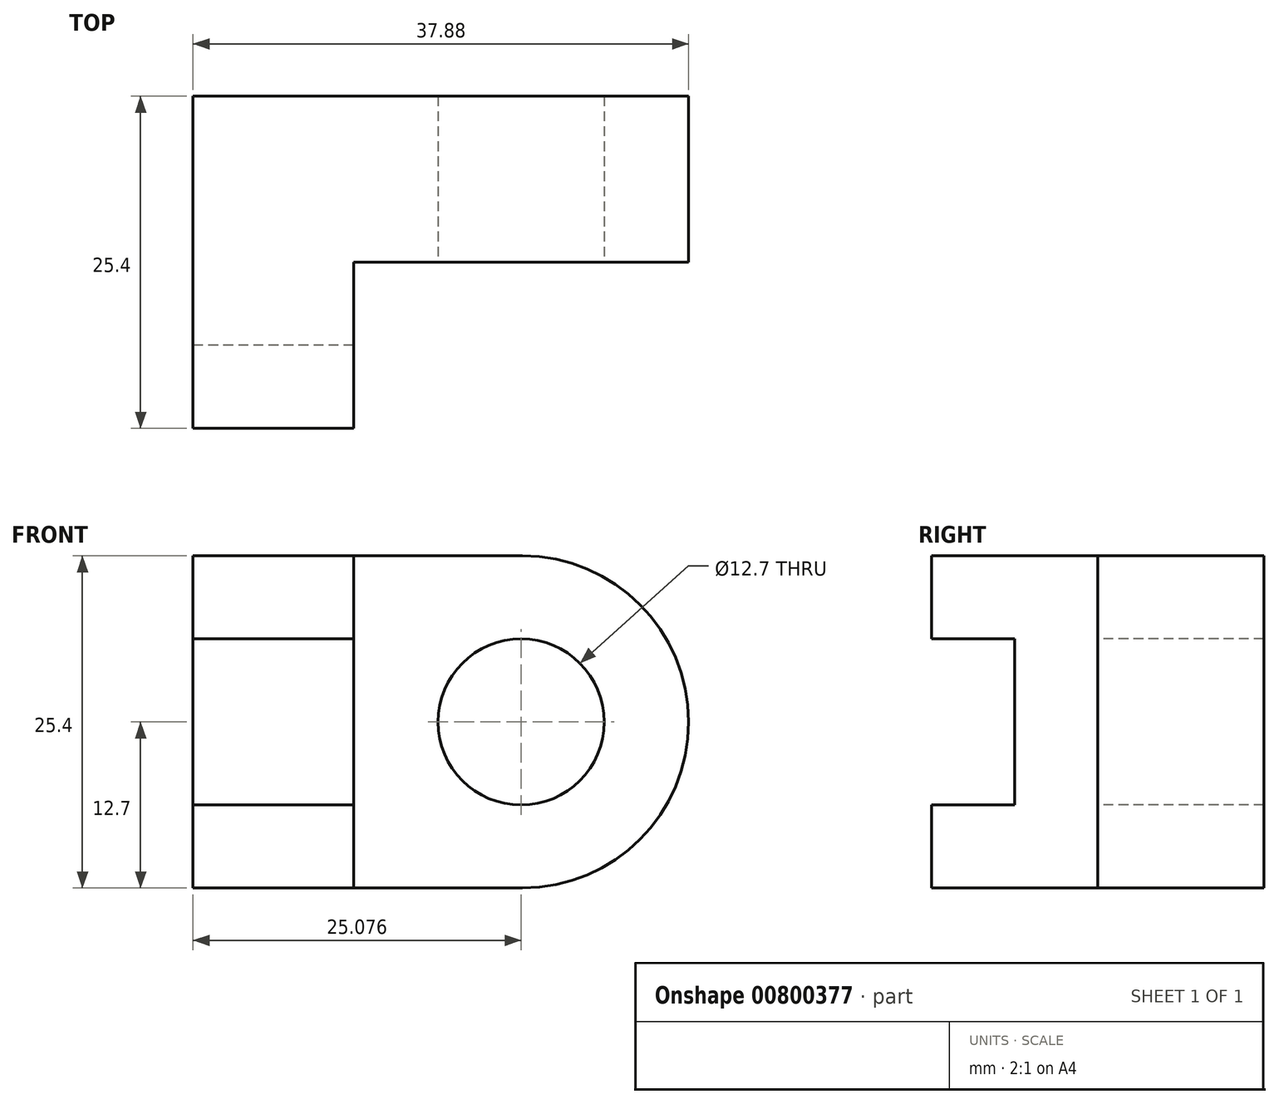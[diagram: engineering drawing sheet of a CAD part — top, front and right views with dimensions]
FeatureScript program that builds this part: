
annotation { "Feature Type Name" : "Feature", "Feature Type Description" : "" }
export const myFeature = defineFeature(function(context is Context, id is Id, definition is map)
    precondition{}
    {
        {
            var Q0;
            Q0=qCreatedBy(makeId("Front.planeOp"),FACE);
            var sketch = newSketch(context, id + "F0", { "sketchPlane" : qUnion([Q0])});
            skLineSegment(sketch, "E0", {"start": v(0, 0) * mm, "end": v(0, 25.4) * mm});
            skLineSegment(sketch, "E1", {"start": v(0, 0) * mm, "end": v(38.1, 0) * mm});
            skLineSegment(sketch, "E2", {"start": v(38.1, 0) * mm, "end": v(38.1, 25.4) * mm});
            skLineSegment(sketch, "E3", {"start": v(0, 25.4) * mm, "end": v(38.1, 25.4) * mm});
            skLineSegment(sketch, "E4", {"start": v(0, 25.4) * mm, "end": v(12.7, 25.4) * mm});
            skSolve(sketch);
        }
        {
            var Q0;
            Q0=makeQuery(id+"F0.imprint","IMPRINT",FACE,{"disambiguationData":[TD([[makeQuery(id+"F0.imprint","IMPRINT",EDGE,{"derivedFrom":sQuery(id+"F0.wireOp",EDGE,"E0")}),-1.0]])]});
            extrude(context, id + "F1", {"entities" : qUnion([Q0]), "depth" : 25.4 * mm, "offsetDistance" : 25.4 * mm});
        }
        {
            var Q0;
            Q0=makeQuery(id+"F1.opExtrude","SWEPT_FACE",FACE,{"disambiguationData":[OSD([sQuery(id+"F0.wireOp",EDGE,"E3"),sQuery(id+"F0.wireOp",EDGE,"E4")])]});
            var sketch = newSketch(context, id + "F2", { "sketchPlane" : qUnion([Q0])});
            skLineSegment(sketch, "E5", {"start": v(12.27, -25.4) * mm, "end": v(12.27, -12.7) * mm});
            skLineSegment(sketch, "E6", {"start": v(12.27, -12.7) * mm, "end": v(38.1, -12.7) * mm});
            skSolve(sketch);
        }
        {
            var Q0;
            {var subQ0=sQuery(id+"F2.wireOp",EDGE,"E5");Q0=makeQuery(id+"F2.imprint","IMPRINT",FACE,{"disambiguationData":[TD([[makeQuery(id+"F2.imprint","IMPRINT",EDGE,{"derivedFrom":subQ0}),-1.0]])]});}
            extrude(context, id + "F3", {"entities" : qUnion([Q0]), "operationType" : NewBodyOperationType.REMOVE, "oppositeDirection" : true, "depth" : 25.4 * mm, "offsetDistance" : 25.4 * mm});
        }
        {
            var Q0;
            Q0=makeQuery(id+"F3.boolean.opBoolean","COPY",FACE,{"derivedFrom":makeQuery(id+"F3.opExtrude","SWEPT_FACE",FACE,{"disambiguationData":[OSD([sQuery(id+"F2.wireOp",EDGE,"E6")])]})});
            var sketch = newSketch(context, id + "F4", { "sketchPlane" : qUnion([Q0])});
            skLineSegment(sketch, "E7", {"start": v(12.27, 25.4) * mm, "end": v(25.18, 25.4) * mm});
            skLineSegment(sketch, "E8", {"start": v(25.18, 25.4) * mm, "end": v(25.18, 0) * mm});
            skArc(sketch, "E9", {"start": v(25.18, 0) * mm, "mid": v(37.88, 12.7) * mm, "end": v(25.18, 25.4) * mm});
            skSolve(sketch);
        }
        {
            var Q0;
            {var subQ0=sQuery(id+"F4.wireOp",EDGE,"E9");Q0=makeQuery(id+"F4.imprint","IMPRINT",FACE,{"disambiguationData":[TD([[makeQuery(id+"F4.imprint","IMPRINT",EDGE,{"derivedFrom":subQ0}),-1.0]])]});}
            extrude(context, id + "F5", {"entities" : qUnion([Q0]), "operationType" : NewBodyOperationType.REMOVE, "oppositeDirection" : true, "depth" : 25.4 * mm, "offsetDistance" : 25.4 * mm});
        }
        {
            var Q0;
            Q0=makeQuery(id+"F3.boolean.opBoolean","COPY",FACE,{"derivedFrom":makeQuery(id+"F3.opExtrude","SWEPT_FACE",FACE,{"disambiguationData":[OSD([sQuery(id+"F2.wireOp",EDGE,"E6")])]})});
            var sketch = newSketch(context, id + "F6", { "sketchPlane" : qUnion([Q0])});
            skLineSegment(sketch, "E10", {"start": v(12.27, 12.7) * mm, "end": v(37.88, 12.7) * mm});
            skCircle(sketch, "E11", {"center": v(25.08, 12.7) * mm, "radius": 6.35 * mm});
            skSolve(sketch);
        }
        {
            var Q0;
            {var subQ0=sQuery(id+"F6.wireOp",EDGE,"E11");var subQ1=sQuery(id+"F6.wireOp",EDGE,"E10");var subQ2=makeQuery(id+"F6.imprint","INTERSECT",VERTEX,{"disambiguationData":[OD(0.0)],"derivedFrom":[subQ1,subQ0]});Q0=makeQuery(id+"F6.imprint","IMPRINT",FACE,{"disambiguationData":[TD([[makeQuery(id+"F6.imprint","IMPRINT",EDGE,{"disambiguationData":[TD([[subQ2,-1.0]])],"derivedFrom":subQ1}),1.0]])]});}
            var Q1;
            {var subQ0=sQuery(id+"F6.wireOp",EDGE,"E11");var subQ1=sQuery(id+"F6.wireOp",EDGE,"E10");var subQ2=makeQuery(id+"F6.imprint","INTERSECT",VERTEX,{"disambiguationData":[OD(0.0)],"derivedFrom":[subQ1,subQ0]});Q1=makeQuery(id+"F6.imprint","IMPRINT",FACE,{"disambiguationData":[TD([[makeQuery(id+"F6.imprint","IMPRINT",EDGE,{"disambiguationData":[TD([[subQ2,-1.0]])],"derivedFrom":subQ1}),-1.0]])]});}
            extrude(context, id + "F7", {"entities" : qUnion([Q0, Q1]), "operationType" : NewBodyOperationType.REMOVE, "oppositeDirection" : true, "depth" : 25.4 * mm, "offsetDistance" : 25.4 * mm});
        }
        {
            var Q0;
            Q0=makeQuery(id+"F1.opExtrude","CAP_FACE",FACE,{"disambiguationData":[OSD([sQuery(id+"F0.wireOp",EDGE,"E0"),sQuery(id+"F0.wireOp",EDGE,"E1"),sQuery(id+"F0.wireOp",EDGE,"E2"),sQuery(id+"F0.wireOp",EDGE,"E3"),sQuery(id+"F0.wireOp",EDGE,"E4")])],"isStart":false});
            var sketch = newSketch(context, id + "F8", { "sketchPlane" : qUnion([Q0])});
            skLineSegment(sketch, "E12", {"start": v(12.27, 25.4) * mm, "end": v(12.27, 19.05) * mm});
            skLineSegment(sketch, "E13", {"start": v(12.27, 19.05) * mm, "end": v(0, 19.05) * mm});
            skLineSegment(sketch, "E14", {"start": v(12.27, 0) * mm, "end": v(12.27, 6.35) * mm});
            skLineSegment(sketch, "E15", {"start": v(12.27, 6.35) * mm, "end": v(0, 6.35) * mm});
            skSolve(sketch);
        }
        {
            var Q0;
            {var subQ0=sQuery(id+"F8.wireOp",EDGE,"E13");Q0=makeQuery(id+"F8.imprint","IMPRINT",FACE,{"disambiguationData":[TD([[makeQuery(id+"F8.imprint","IMPRINT",EDGE,{"derivedFrom":subQ0}),1.0]])]});}
            extrude(context, id + "F9", {"entities" : qUnion([Q0]), "operationType" : NewBodyOperationType.REMOVE, "oppositeDirection" : true, "depth" : 6.35 * mm, "offsetDistance" : 25.4 * mm});
        }
    });
